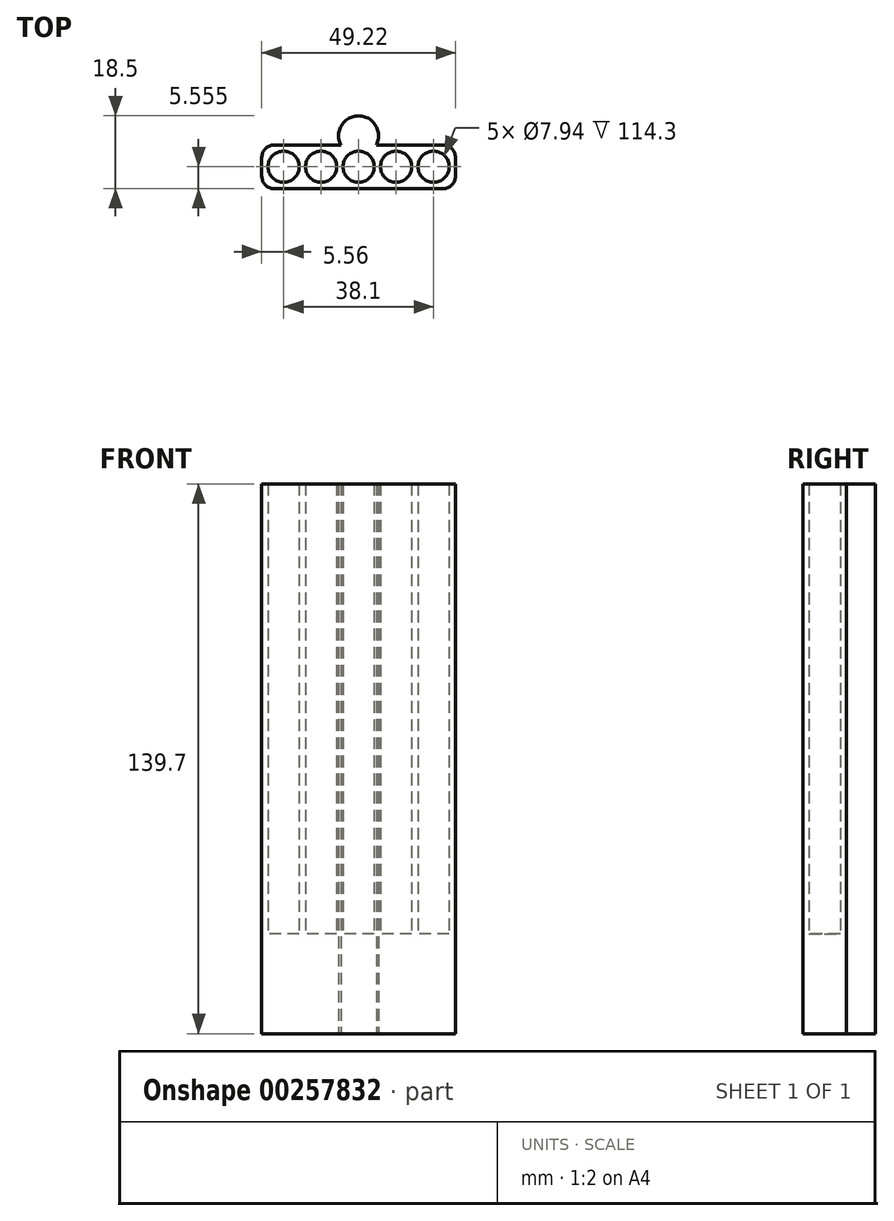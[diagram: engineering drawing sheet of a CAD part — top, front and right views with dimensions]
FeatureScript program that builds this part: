
annotation { "Feature Type Name" : "Feature", "Feature Type Description" : "" }
export const myFeature = defineFeature(function(context is Context, id is Id, definition is map)
    precondition{}
    {
        {
            var Q0;
            Q0=qCreatedBy(makeId("Top.planeOp"),FACE);
            var sketch = newSketch(context, id + "F0", { "sketchPlane" : qUnion([Q0])});
            skArc(sketch, "E0", {"start": v(4.52, -44.22) * mm, "mid": v(31.43, -31.43) * mm, "end": v(44.22, -4.52) * mm});
            skArc(sketch, "E1", {"start": v(-4.52, 44.22) * mm, "mid": v(0, 36.83) * mm, "end": v(4.52, 44.22) * mm});
            skArc(sketch, "E2", {"start": v(44.22, 4.52) * mm, "mid": v(36.83, 0) * mm, "end": v(44.22, -4.52) * mm});
            skArc(sketch, "E3", {"start": v(4.52, -44.22) * mm, "mid": v(0, -36.83) * mm, "end": v(-4.52, -44.22) * mm});
            skArc(sketch, "E4", {"start": v(-44.22, -4.52) * mm, "mid": v(-36.83, 0) * mm, "end": v(-44.22, 4.52) * mm});
            skArc(sketch, "E5.trimOffspring", {"start": v(44.22, 4.52) * mm, "mid": v(31.43, 31.43) * mm, "end": v(4.52, 44.22) * mm});
            skArc(sketch, "E6.trimOffspring", {"start": v(-4.52, 44.22) * mm, "mid": v(-31.43, 31.43) * mm, "end": v(-44.22, 4.52) * mm});
            skArc(sketch, "E7.trimOffspring", {"start": v(-44.22, -4.52) * mm, "mid": v(-31.43, -31.43) * mm, "end": v(-4.52, -44.22) * mm});
            skLineSegment(sketch, "E8", {"start": v(-24.6, -44.22) * mm, "end": v(-24.6, -55.33) * mm});
            skLineSegment(sketch, "E9", {"start": v(24.6, -44.22) * mm, "end": v(24.6, -55.33) * mm});
            skLineSegment(sketch, "E10", {"start": v(-24.6, -55.33) * mm, "end": v(24.6, -55.33) * mm});
            skPoint(sketch, "E11", {"position": v(-24.6, -49.78) * mm});
            skLineSegment(sketch, "E12", {"start": v(-24.6, -44.22) * mm, "end": v(-4.52, -44.22) * mm});
            skPoint(sketch, "E13", {"position": v(0, -55.33) * mm});
            skCircle(sketch, "E14", {"center": v(-19.05, -49.78) * mm, "radius": 3.97 * mm});
            skCircle(sketch, "E15", {"center": v(-9.53, -49.78) * mm, "radius": 3.97 * mm});
            skCircle(sketch, "E16", {"center": v(0, -49.78) * mm, "radius": 3.97 * mm});
            skCircle(sketch, "E17", {"center": v(9.52, -49.78) * mm, "radius": 3.97 * mm});
            skCircle(sketch, "E18", {"center": v(19.05, -49.78) * mm, "radius": 3.97 * mm});
            skPoint(sketch, "E19", {"position": v(-23.02, -49.78) * mm});
            skPoint(sketch, "E20", {"position": v(-15.08, -49.78) * mm});
            skPoint(sketch, "E21", {"position": v(-13.5, -49.78) * mm});
            skPoint(sketch, "E22", {"position": v(-5.56, -49.78) * mm});
            skPoint(sketch, "E23", {"position": v(-3.97, -49.78) * mm});
            skPoint(sketch, "E24", {"position": v(3.97, -49.78) * mm});
            skPoint(sketch, "E25", {"position": v(5.56, -49.78) * mm});
            skPoint(sketch, "E26", {"position": v(13.5, -49.78) * mm});
            skPoint(sketch, "E27", {"position": v(15.08, -49.78) * mm});
            skPoint(sketch, "E28", {"position": v(23.02, -49.78) * mm});
            skPoint(sketch, "E29", {"position": v(24.6, -49.78) * mm});
            skLineSegment(sketch, "E30.trimOffspring", {"start": v(4.52, -44.22) * mm, "end": v(24.6, -44.22) * mm});
            skSolve(sketch);
        }
        {
            var Q0;
            Q0=makeQuery(id+"F0.imprint","IMPRINT",FACE,{"disambiguationData":[TD([[makeQuery(id+"F0.imprint","IMPRINT",EDGE,{"derivedFrom":sQuery(id+"F0.wireOp",EDGE,"E3")}),1.0]])]});
            extrude(context, id + "F1", {"entities" : qUnion([Q0]), "depth" : 139.7 * mm});
        }
        {
            var Q0;
            Q0=makeQuery(id+"F0.imprint","IMPRINT",FACE,{"disambiguationData":[TD([[makeQuery(id+"F0.imprint","IMPRINT",EDGE,{"derivedFrom":sQuery(id+"F0.wireOp",EDGE,"E14")}),1.0]])]});
            var Q1;
            Q1=makeQuery(id+"F0.imprint","IMPRINT",FACE,{"disambiguationData":[TD([[makeQuery(id+"F0.imprint","IMPRINT",EDGE,{"derivedFrom":sQuery(id+"F0.wireOp",EDGE,"E15")}),1.0]])]});
            var Q2;
            Q2=makeQuery(id+"F0.imprint","IMPRINT",FACE,{"disambiguationData":[TD([[makeQuery(id+"F0.imprint","IMPRINT",EDGE,{"derivedFrom":sQuery(id+"F0.wireOp",EDGE,"E16")}),1.0]])]});
            var Q3;
            Q3=makeQuery(id+"F0.imprint","IMPRINT",FACE,{"disambiguationData":[TD([[makeQuery(id+"F0.imprint","IMPRINT",EDGE,{"derivedFrom":sQuery(id+"F0.wireOp",EDGE,"E17")}),1.0]])]});
            var Q4;
            Q4=makeQuery(id+"F0.imprint","IMPRINT",FACE,{"disambiguationData":[TD([[makeQuery(id+"F0.imprint","IMPRINT",EDGE,{"derivedFrom":sQuery(id+"F0.wireOp",EDGE,"E18")}),1.0]])]});
            extrude(context, id + "F2", {"entities" : qUnion([Q0, Q1, Q2, Q3, Q4]), "operationType" : NewBodyOperationType.ADD, "depth" : 25.4 * mm});
        }
        {
            var Q0;
            Q0=makeQuery(id+"F1.opExtrude","SWEPT_EDGE",EDGE,{"disambiguationData":[OSD([sQuery(id+"F0.wireOp",EDGE,"E9"),sQuery(id+"F0.wireOp",EDGE,"E10")])]});
            var Q1;
            Q1=makeQuery(id+"F1.opExtrude","SWEPT_EDGE",EDGE,{"disambiguationData":[OSD([sQuery(id+"F0.wireOp",EDGE,"E9"),sQuery(id+"F0.wireOp",EDGE,"E30.trimOffspring")])]});
            var Q2;
            Q2=makeQuery(id+"F1.opExtrude","SWEPT_EDGE",EDGE,{"disambiguationData":[OSD([sQuery(id+"F0.wireOp",EDGE,"E8"),sQuery(id+"F0.wireOp",EDGE,"E12")])]});
            var Q3;
            Q3=makeQuery(id+"F1.opExtrude","SWEPT_EDGE",EDGE,{"disambiguationData":[OSD([sQuery(id+"F0.wireOp",EDGE,"E8"),sQuery(id+"F0.wireOp",EDGE,"E10")])]});
            fillet(context, id + "F3", {"entities" : qUnion([Q0, Q1, Q2, Q3]), "radius" : 3.17 * mm, "tangentPropagation" : true, "allowEdgeOverflow" : false});
        }
    });
